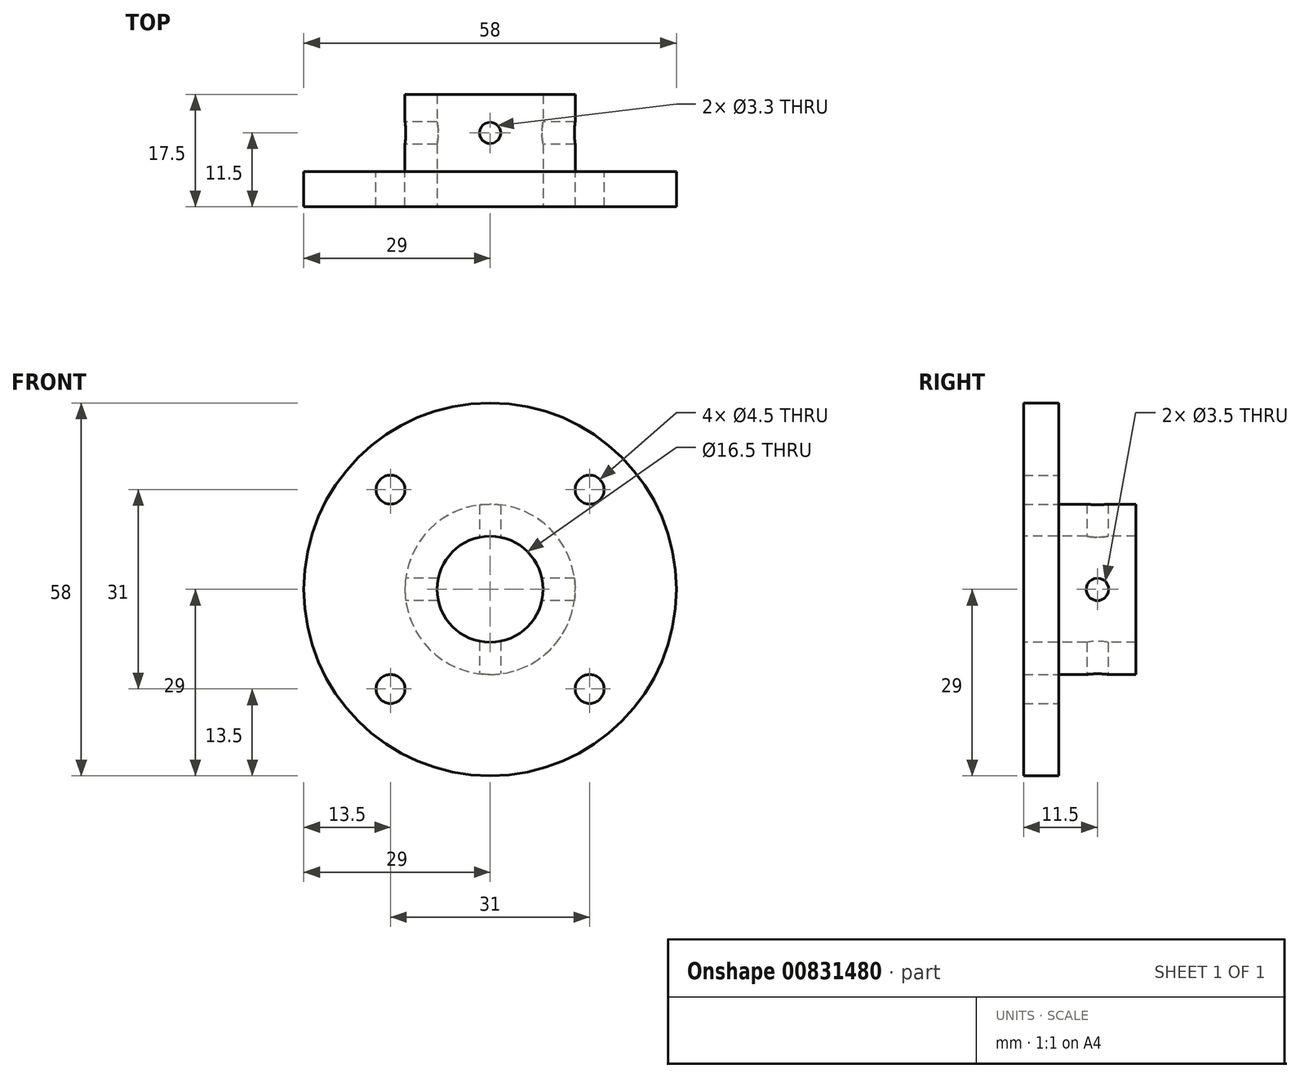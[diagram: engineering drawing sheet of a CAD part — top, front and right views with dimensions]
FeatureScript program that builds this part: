
annotation { "Feature Type Name" : "Feature", "Feature Type Description" : "" }
export const myFeature = defineFeature(function(context is Context, id is Id, definition is map)
    precondition{}
    {
        {
            var Q0;
            Q0=qCreatedBy(makeId("Right.planeOp"),FACE);
            var sketch = newSketch(context, id + "F0", { "sketchPlane" : qUnion([Q0])});
            skLineSegment(sketch, "E0", {"start": v(0, 8.25) * mm, "end": v(0, 29) * mm});
            skLineSegment(sketch, "E1", {"start": v(0, 29) * mm, "end": v(5.5, 29) * mm});
            skLineSegment(sketch, "E2", {"start": v(5.5, 29) * mm, "end": v(5.5, 13.25) * mm});
            skLineSegment(sketch, "E3", {"start": v(5.5, 13.25) * mm, "end": v(17.5, 13.25) * mm});
            skLineSegment(sketch, "E4", {"start": v(17.5, 13.25) * mm, "end": v(17.5, 8.25) * mm});
            skLineSegment(sketch, "E5", {"start": v(17.5, 8.25) * mm, "end": v(0, 8.25) * mm});
            skLineSegment(sketch, "E6", {"start": v(0, 0) * mm, "end": v(10.68, 0) * mm});
            skLineSegment(sketch, "E7.MirrorCS", {"start": v(0, -29) * mm, "end": v(5.5, -29) * mm});
            skLineSegment(sketch, "E8.MirrorCS", {"start": v(5.5, -29) * mm, "end": v(5.5, -13.25) * mm});
            skLineSegment(sketch, "E9.MirrorCS", {"start": v(17.5, -13.25) * mm, "end": v(17.5, -8.25) * mm});
            skLineSegment(sketch, "E10.MirrorCS", {"start": v(0, -8.25) * mm, "end": v(0, -29) * mm});
            skLineSegment(sketch, "E11.MirrorCS", {"start": v(17.5, -8.25) * mm, "end": v(0, -8.25) * mm});
            skLineSegment(sketch, "E12.MirrorCS", {"start": v(5.5, -13.25) * mm, "end": v(17.5, -13.25) * mm});
            skSolve(sketch);
        }
        {
            var Q0;
            Q0=makeQuery(id+"F0.imprint","IMPRINT",FACE,{"disambiguationData":[TD([[makeQuery(id+"F0.imprint","IMPRINT",EDGE,{"derivedFrom":sQuery(id+"F0.wireOp",EDGE,"E0")}),-1.0]])]});
            var Q1;
            Q1=sQuery(id+"F0.wireOp",EDGE,"E6");
            revolve(context, id + "F1", {"entities" : qUnion([Q0]), "axis" : qUnion([Q1]), "revolveType" : RevolveType.FULL});
        }
        {
            var Q0;
            Q0=makeQuery(id+"F1.opRevolve","SWEPT_EDGE",EDGE,{"disambiguationData":[OSD([sQuery(id+"F0.wireOp",EDGE,"E2"),sQuery(id+"F0.wireOp",EDGE,"E3")])]});
            fillet(context, id + "F2", {"entities" : qUnion([Q0]), "radius" : 0.25 * mm, "tangentPropagation" : true, "allowEdgeOverflow" : false});
        }
        {
            var Q0;
            Q0=makeQuery(id+"F1.opRevolve","SWEPT_FACE",FACE,{"disambiguationData":[OSD([sQuery(id+"F0.wireOp",EDGE,"E2")])]});
            var sketch = newSketch(context, id + "F3", { "sketchPlane" : qUnion([Q0])});
            skCircle(sketch, "E13", {"center": v(-15.5, 15.5) * mm, "radius": 2.25 * mm});
            skCircle(sketch, "E14", {"center": v(15.5, 15.5) * mm, "radius": 2.25 * mm});
            skCircle(sketch, "E15", {"center": v(-15.5, -15.5) * mm, "radius": 2.25 * mm});
            skCircle(sketch, "E16", {"center": v(15.5, -15.5) * mm, "radius": 2.25 * mm});
            skSolve(sketch);
        }
        {
            var Q0;
            Q0=qSketchRegion(id+"F3",true);
            extrude(context, id + "F4", {"entities" : qUnion([Q0]), "operationType" : NewBodyOperationType.REMOVE, "oppositeDirection" : true, "depth" : 25 * mm, "offsetDistance" : 25 * mm});
        }
        {
            var Q0;
            Q0=qCreatedBy(makeId("Top.planeOp"),FACE);
            var sketch = newSketch(context, id + "F5", { "sketchPlane" : qUnion([Q0])});
            skCircle(sketch, "E17", {"center": v(0, 11.5) * mm, "radius": 1.65 * mm});
            skSolve(sketch);
        }
        {
            var Q0;
            Q0=qSketchRegion(id+"F5",true);
            extrude(context, id + "F6", {"entities" : qUnion([Q0]), "operationType" : NewBodyOperationType.REMOVE, "depth" : 25 * mm, "offsetDistance" : 25 * mm, "hasSecondDirection" : true, "secondDirectionOppositeDirection" : true, "secondDirectionDepth" : 25 * mm});
        }
        {
            var Q0;
            Q0=qCreatedBy(makeId("Right.planeOp"),FACE);
            var sketch = newSketch(context, id + "F7", { "sketchPlane" : qUnion([Q0])});
            skCircle(sketch, "E18", {"center": v(11.5, 0) * mm, "radius": 1.75 * mm});
            skSolve(sketch);
        }
        {
            var Q0;
            Q0=qSketchRegion(id+"F7",true);
            extrude(context, id + "F8", {"entities" : qUnion([Q0]), "operationType" : NewBodyOperationType.REMOVE, "depth" : 25 * mm, "offsetDistance" : 25 * mm, "hasSecondDirection" : true, "secondDirectionOppositeDirection" : true, "secondDirectionDepth" : 25 * mm});
        }
    });
